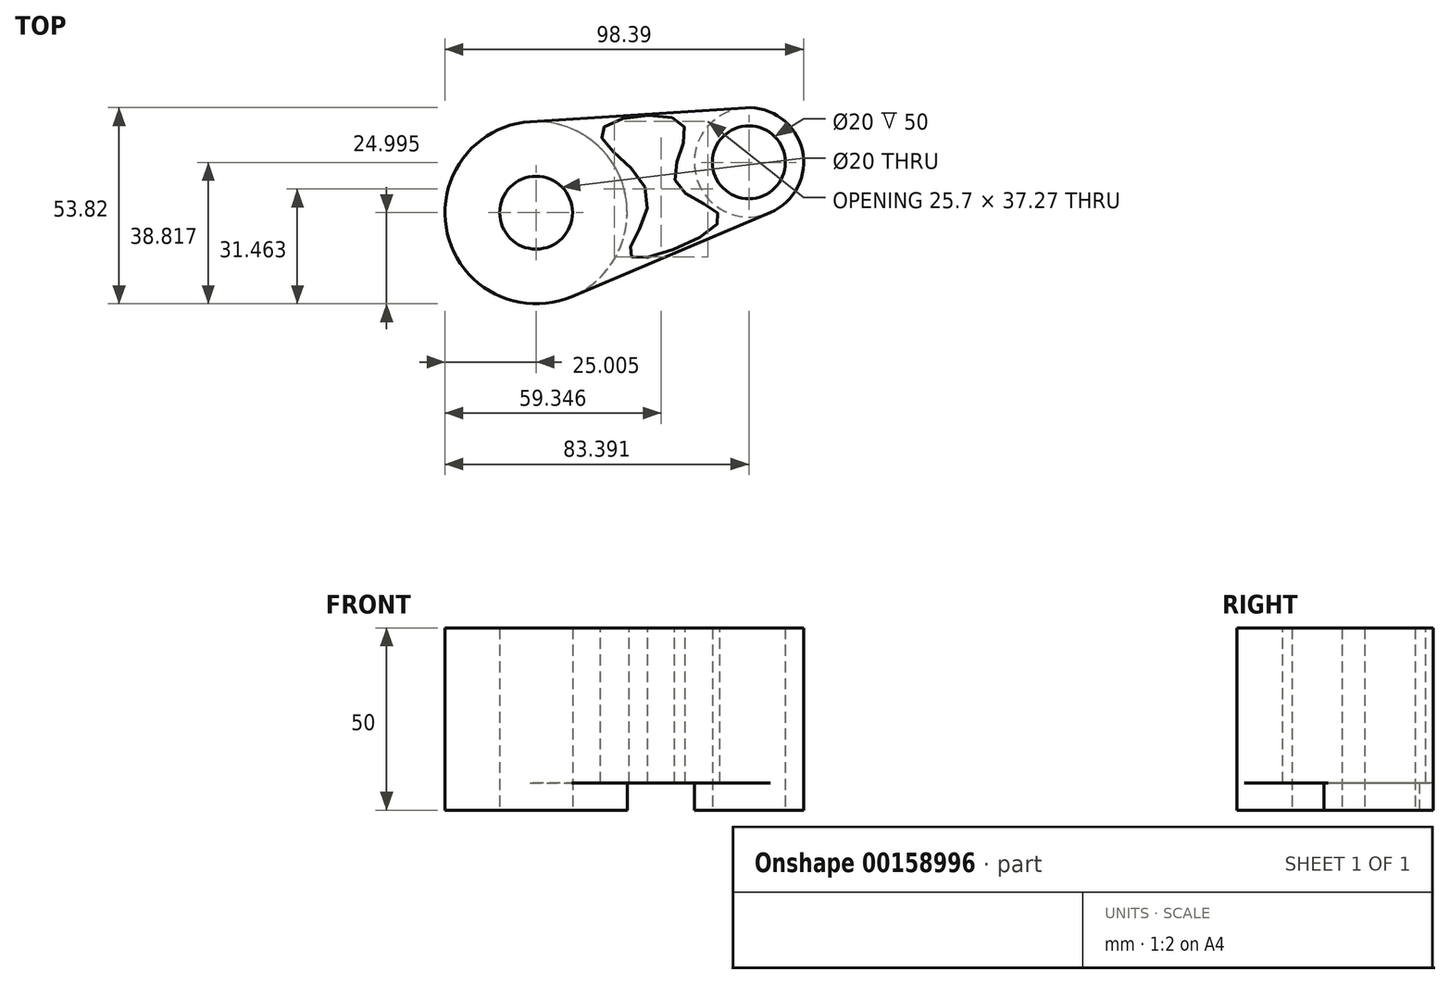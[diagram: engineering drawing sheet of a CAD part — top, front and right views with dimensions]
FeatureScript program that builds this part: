
annotation { "Feature Type Name" : "Feature", "Feature Type Description" : "" }
export const myFeature = defineFeature(function(context is Context, id is Id, definition is map)
    precondition{}
    {
        {
            var Q0;
            Q0=qCreatedBy(makeId("Top.planeOp"),FACE);
            var sketch = newSketch(context, id + "F0", { "sketchPlane" : qUnion([Q0])});
            skCircle(sketch, "E0", {"center": v(-40.12, 12.17) * mm, "radius": 25 * mm});
            skCircle(sketch, "E1", {"center": v(18.27, 25.99) * mm, "radius": 15 * mm});
            skLineSegment(sketch, "E2", {"start": v(-41.74, 37.11) * mm, "end": v(17.3, 40.96) * mm});
            skLineSegment(sketch, "E3", {"start": v(-30.38, -10.86) * mm, "end": v(24.11, 12.17) * mm});
            skCircle(sketch, "E4", {"center": v(-40.12, 12.17) * mm, "radius": 10 * mm});
            skCircle(sketch, "E5", {"center": v(18.27, 25.99) * mm, "radius": 10 * mm});
            skFitSpline(sketch, "E6", {"points": [v(-14, 0) * mm, v(-9.56, 16.9) * mm, v(-22.28, 34.66) * mm, v(0, 36.73) * mm, v(-1.71, 20.31) * mm, v(10.27, 10.4) * mm, v(-14, 0) * mm]});
            skSolve(sketch);
        }
        {
            var Q0;
            Q0 = qSketchRegion(id + "F0", true);
            extrude(context, id + "F1", {"entities" : qUnion([Q0]), "depth" : 50 * mm});
        }
        {
            var Q0;
            {var subQ1=sQuery(id+"F0.wireOp",EDGE,"E2");Q0=makeQuery(id+"F0.imprint","IMPRINT",FACE,{"disambiguationData":[TD([[makeQuery(id+"F0.imprint","IMPRINT",EDGE,{"derivedFrom":subQ1}),-1.0]])]});}
            extrude(context, id + "F2", {"entities" : qUnion([Q0]), "operationType" : NewBodyOperationType.REMOVE, "endBound" : BoundingType.SYMMETRIC, "depth" : 15 * mm});
        }
    });
